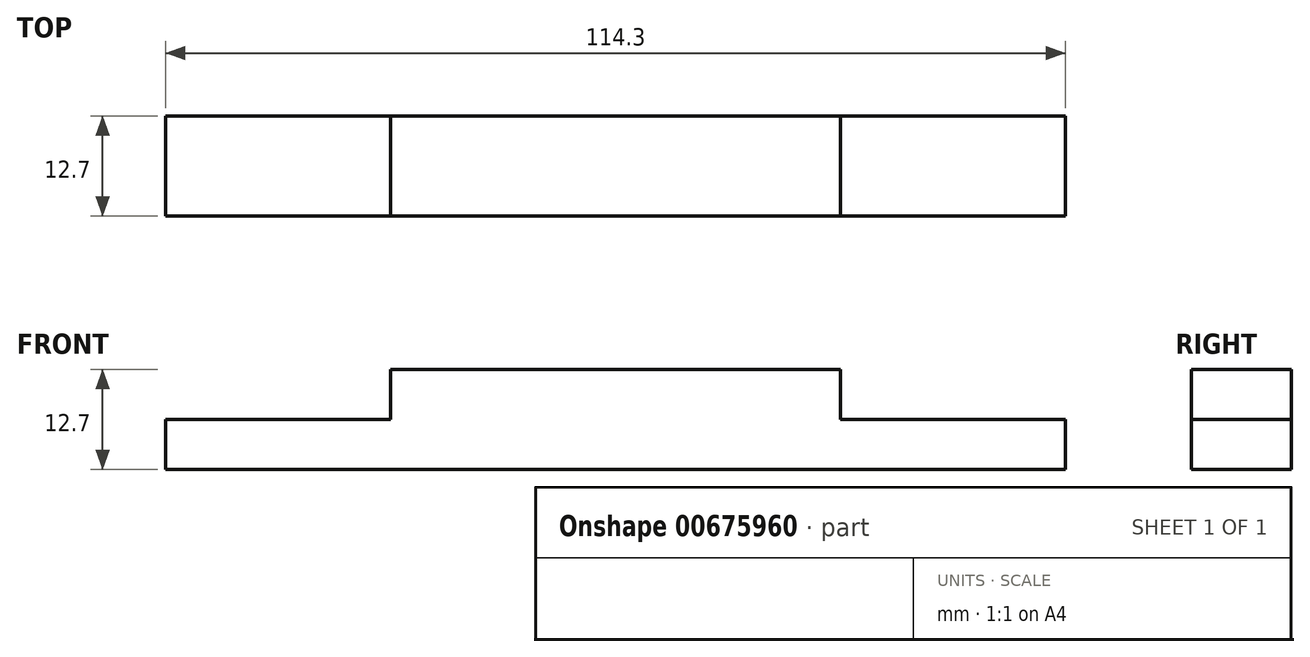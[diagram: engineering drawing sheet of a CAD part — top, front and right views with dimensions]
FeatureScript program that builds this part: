
annotation { "Feature Type Name" : "Feature", "Feature Type Description" : "" }
export const myFeature = defineFeature(function(context is Context, id is Id, definition is map)
    precondition{}
    {
        {
            var Q0;
            Q0=qCreatedBy(makeId("Front.planeOp"),FACE);
            var sketch = newSketch(context, id + "F0", { "sketchPlane" : qUnion([Q0])});
            skLineSegment(sketch, "E0.bottom", {"start": v(-13.08, -1.93) * mm, "end": v(44.07, -1.93) * mm});
            skLineSegment(sketch, "E0.top", {"start": v(-41.65, -14.63) * mm, "end": v(72.65, -14.63) * mm});
            skLineSegment(sketch, "E0.left", {"start": v(-41.65, -8.28) * mm, "end": v(-41.65, -14.63) * mm});
            skLineSegment(sketch, "E0.right", {"start": v(72.65, -8.28) * mm, "end": v(72.65, -14.63) * mm});
            skLineSegment(sketch, "E1", {"start": v(-41.65, -8.28) * mm, "end": v(72.65, -8.28) * mm});
            skLineSegment(sketch, "E2.top", {"start": v(-13.08, -8.28) * mm, "end": v(44.07, -8.28) * mm});
            skLineSegment(sketch, "E2.left", {"start": v(-13.08, -1.93) * mm, "end": v(-13.08, -8.28) * mm});
            skLineSegment(sketch, "E2.right", {"start": v(44.07, -1.93) * mm, "end": v(44.07, -8.28) * mm});
            skLineSegment(sketch, "E3", {"start": v(15.5, -8.28) * mm, "end": v(15.5, -14.63) * mm});
            skSolve(sketch);
        }
        {
            var Q0;
            Q0 = qSketchRegion(id + "F0", true);
            extrude(context, id + "F1", {"entities" : qUnion([Q0]), "depth" : 12.7 * mm, "offsetDistance" : 25.4 * mm});
        }
    });
